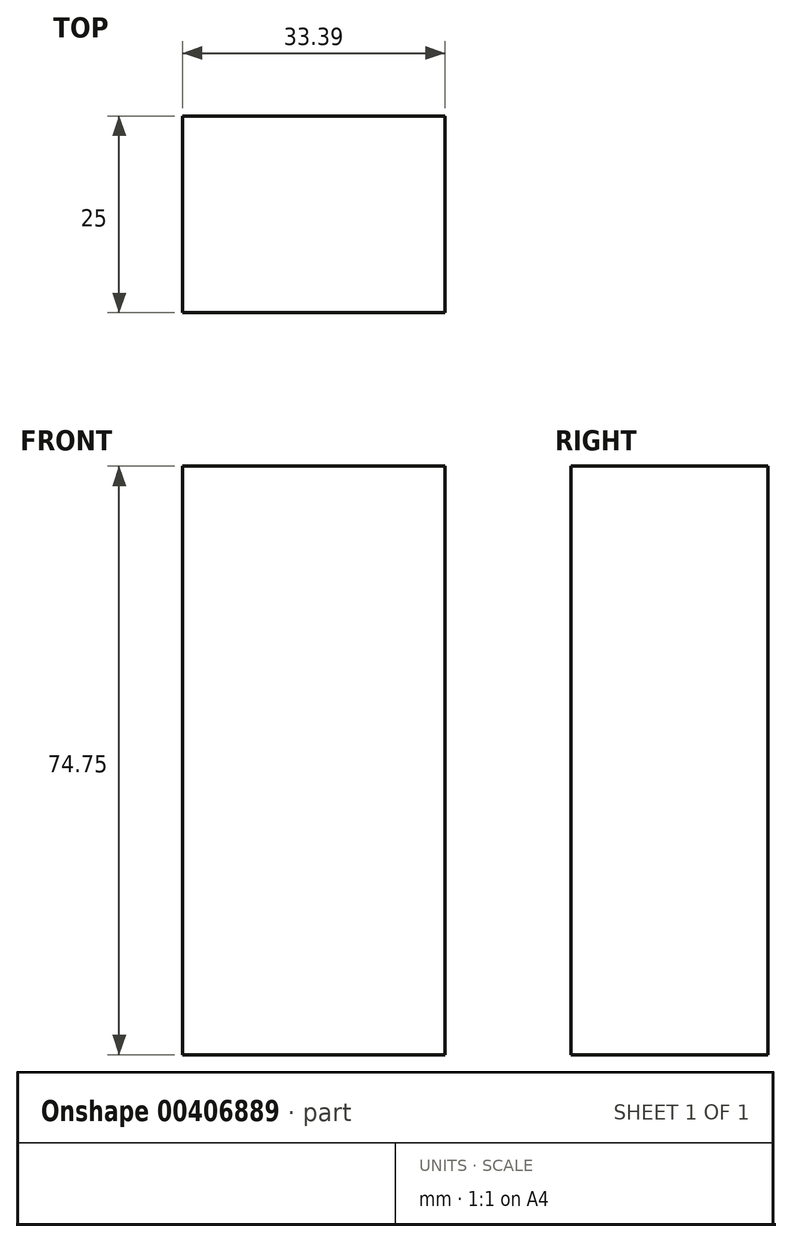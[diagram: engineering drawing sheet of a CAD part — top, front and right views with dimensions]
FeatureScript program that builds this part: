
annotation { "Feature Type Name" : "Feature", "Feature Type Description" : "" }
export const myFeature = defineFeature(function(context is Context, id is Id, definition is map)
    precondition{}
    {
        {
            var Q0;
            Q0=qCreatedBy(makeId("Front.planeOp"),FACE);
            var sketch = newSketch(context, id + "F0", { "sketchPlane" : qUnion([Q0])});
            skLineSegment(sketch, "E0.bottom", {"start": v(-62.53, 74.75) * mm, "end": v(-29.14, 74.75) * mm});
            skLineSegment(sketch, "E0.top", {"start": v(-62.53, 0) * mm, "end": v(-29.14, 0) * mm});
            skLineSegment(sketch, "E0.left", {"start": v(-62.53, 74.75) * mm, "end": v(-62.53, 0) * mm});
            skLineSegment(sketch, "E0.right", {"start": v(-29.14, 74.75) * mm, "end": v(-29.14, 0) * mm});
            skSolve(sketch);
        }
        {
            var Q0;
            Q0 = qSketchRegion(id + "F0", true);
            extrude(context, id + "F1", {"entities" : qUnion([Q0]), "depth" : 25 * mm});
        }
    });
